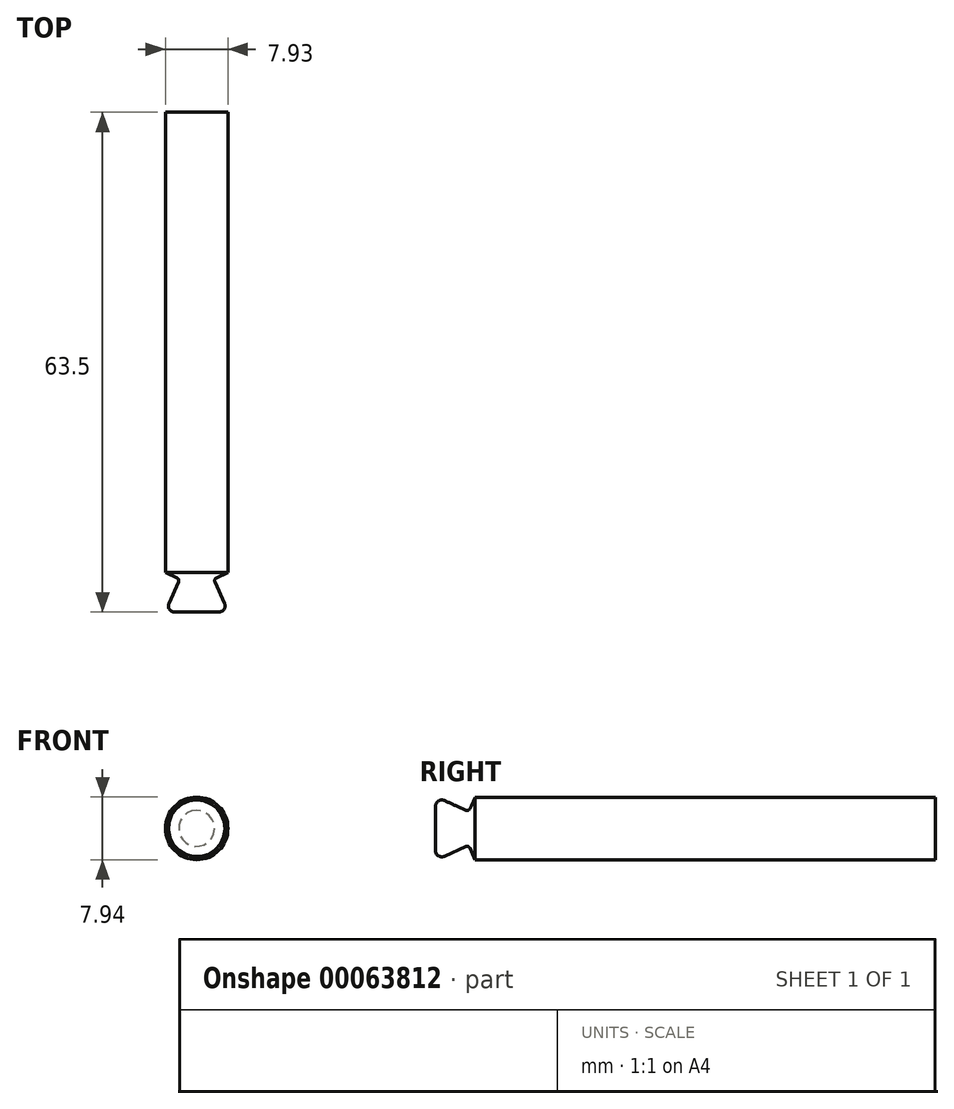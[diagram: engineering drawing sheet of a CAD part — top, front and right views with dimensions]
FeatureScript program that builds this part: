
annotation { "Feature Type Name" : "Feature", "Feature Type Description" : "" }
export const myFeature = defineFeature(function(context is Context, id is Id, definition is map)
    precondition{}
    {
        {
            var Q0;
            Q0=qCreatedBy(makeId("Top.planeOp"),FACE);
            var sketch = newSketch(context, id + "F0", { "sketchPlane" : qUnion([Q0])});
            skLineSegment(sketch, "E0", {"start": v(-1.98, -26.74) * mm, "end": v(-1.98, 31.75) * mm});
            skLineSegment(sketch, "E1", {"start": v(-1.98, 31.75) * mm, "end": v(1.98, 31.75) * mm});
            skArc(sketch, "E2", {"start": v(-0.33, -27.9) * mm, "mid": v(-0.32, -27.6) * mm, "end": v(-0.52, -27.39) * mm});
            skLineSegment(sketch, "E3", {"start": v(-0.84, -31.75) * mm, "end": v(1.98, -31.75) * mm});
            skArc(sketch, "E4", {"start": v(-1.55, -30.64) * mm, "mid": v(-1.5, -31.4) * mm, "end": v(-0.84, -31.75) * mm});
            skLineSegment(sketch, "E5", {"start": v(-0.33, -27.9) * mm, "end": v(-1.55, -30.64) * mm});
            skLineSegment(sketch, "E6", {"start": v(-0.52, -27.39) * mm, "end": v(-1.98, -26.74) * mm});
            skSolve(sketch);
        }
        {
            var Q0;
            Q0=qCreatedBy(makeId("Top.planeOp"),FACE);
            var sketch = newSketch(context, id + "F1", { "sketchPlane" : qUnion([Q0])});
            skLineSegment(sketch, "E7.0", {"start": v(-0.84, -31.75) * mm, "end": v(1.98, -31.75) * mm});
            skArc(sketch, "E7.1", {"start": v(-1.55, -30.64) * mm, "mid": v(-1.5, -31.4) * mm, "end": v(-0.84, -31.75) * mm});
            skLineSegment(sketch, "E7.2", {"start": v(-0.33, -27.9) * mm, "end": v(-1.55, -30.64) * mm});
            skArc(sketch, "E7.3", {"start": v(-0.33, -27.9) * mm, "mid": v(-0.32, -27.6) * mm, "end": v(-0.52, -27.39) * mm});
            skLineSegment(sketch, "E7.4", {"start": v(-0.52, -27.39) * mm, "end": v(-1.98, -26.74) * mm});
            skLineSegment(sketch, "E7.5", {"start": v(-1.98, -26.74) * mm, "end": v(-1.98, 31.75) * mm});
            skLineSegment(sketch, "E7.6", {"start": v(-1.98, 31.75) * mm, "end": v(1.98, 31.75) * mm});
            skLineSegment(sketch, "E8", {"start": v(1.98, 31.75) * mm, "end": v(1.98, -31.75) * mm});
            skLineSegment(sketch, "E9", {"start": v(-1.62, -27.8) * mm, "end": v(-1.62, -34.25) * mm, "construction": true});
            skLineSegment(sketch, "E10", {"start": v(-0.52, -27.39) * mm, "end": v(-0.17, -27.54) * mm, "construction": true});
            skLineSegment(sketch, "E11", {"start": v(-0.17, -27.54) * mm, "end": v(-0.33, -27.9) * mm, "construction": true});
            skLineSegment(sketch, "E12.MirrorCS", {"start": v(4.3, -27.9) * mm, "end": v(5.52, -30.64) * mm, "construction": true});
            skLineSegment(sketch, "E13", {"start": v(-0.84, -31.75) * mm, "end": v(-2.05, -31.75) * mm, "construction": true});
            skLineSegment(sketch, "E14", {"start": v(-2.05, -31.75) * mm, "end": v(-1.5, -30.54) * mm, "construction": true});
            skSolve(sketch);
        }
        {
            var Q0;
            Q0=makeQuery(id+"F1.imprint","IMPRINT",FACE,{"disambiguationData":[TD([[makeQuery(id+"F1.imprint","IMPRINT",EDGE,{"derivedFrom":sQuery(id+"F1.wireOp",EDGE,"E7.0")}),1.0]])]});
            var Q1;
            Q1=sQuery(id+"F1.wireOp",EDGE,"E8");
            revolve(context, id + "F2", {"surfaceOperationType" : NewSurfaceOperationType.NEW, "entities" : qUnion([Q0]), "axis" : qUnion([Q1]), "revolveType" : RevolveType.FULL});
        }
    });
